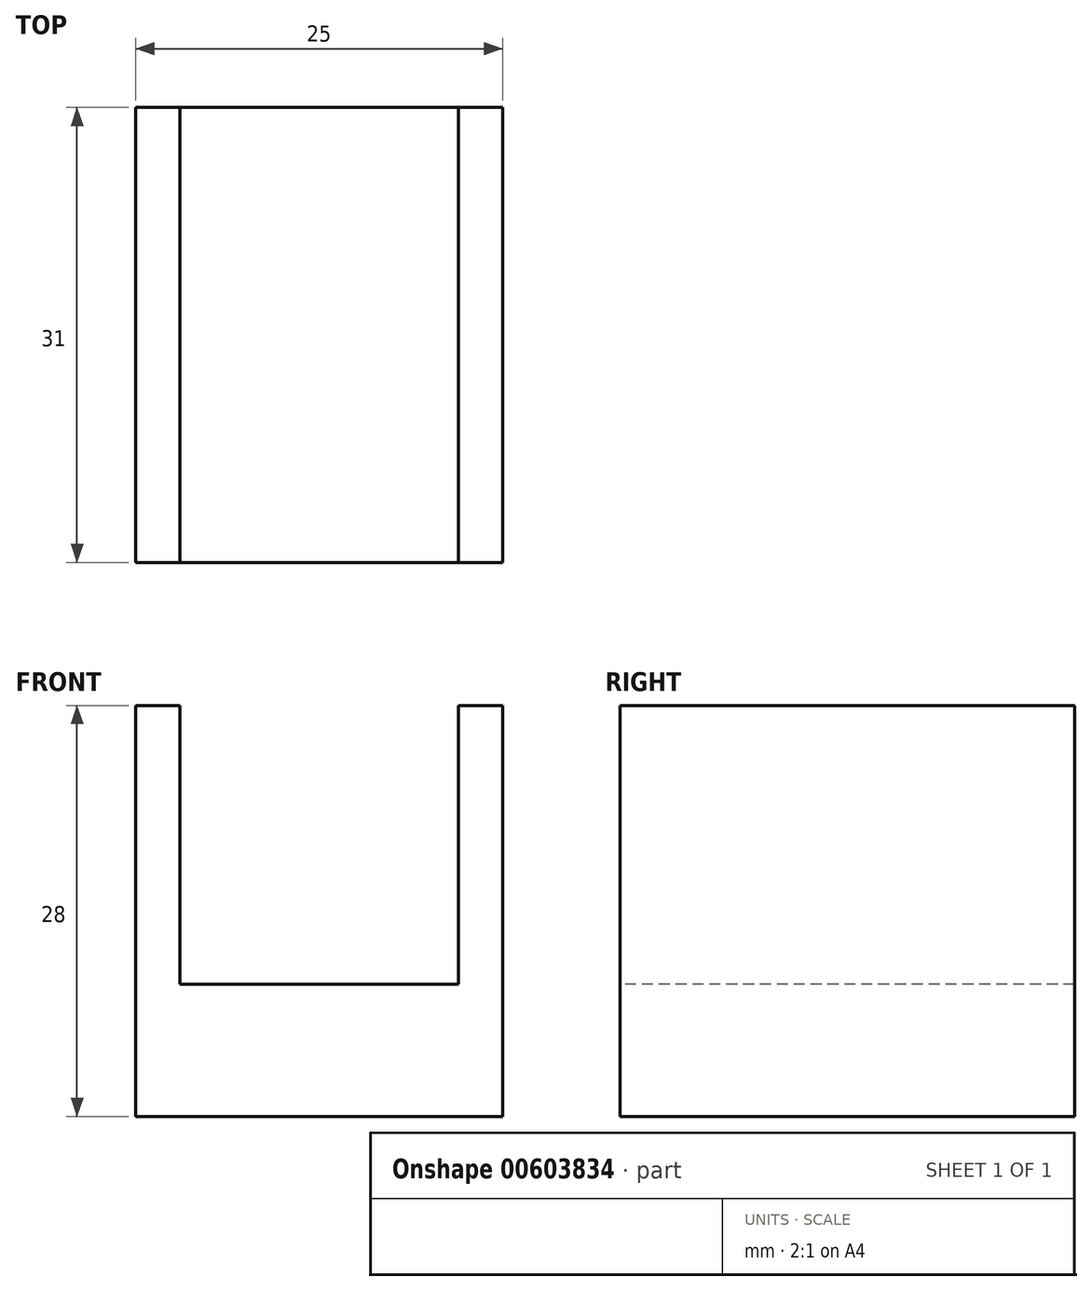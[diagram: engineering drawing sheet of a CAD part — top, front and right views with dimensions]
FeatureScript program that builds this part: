
annotation { "Feature Type Name" : "Feature", "Feature Type Description" : "" }
export const myFeature = defineFeature(function(context is Context, id is Id, definition is map)
    precondition{}
    {
        {
            var Q0;
            Q0=qCreatedBy(makeId("Top.planeOp"),FACE);
            var sketch = newSketch(context, id + "F0", { "sketchPlane" : qUnion([Q0])});
            skLineSegment(sketch, "E0.bottom", {"start": v(0, 0) * mm, "end": v(25, 0) * mm});
            skLineSegment(sketch, "E0.top", {"start": v(0, 31) * mm, "end": v(25, 31) * mm});
            skLineSegment(sketch, "E0.left", {"start": v(0, 0) * mm, "end": v(0, 31) * mm});
            skLineSegment(sketch, "E0.right", {"start": v(25, 0) * mm, "end": v(25, 31) * mm});
            skSolve(sketch);
        }
        {
            var Q0;
            Q0=makeQuery(id+"F0.imprint","IMPRINT",FACE,{"disambiguationData":[TD([[makeQuery(id+"F0.imprint","IMPRINT",EDGE,{"derivedFrom":sQuery(id+"F0.wireOp",EDGE,"E0.bottom")}),1.0]])]});
            extrude(context, id + "F1", {"entities" : qUnion([Q0]), "depth" : 28 * mm, "offsetDistance" : 25 * mm});
        }
        {
            var Q0;
            Q0=makeQuery(id+"F1.opExtrude","SWEPT_FACE",FACE,{"disambiguationData":[OSD([sQuery(id+"F0.wireOp",EDGE,"E0.bottom")])]});
            var sketch = newSketch(context, id + "F2", { "sketchPlane" : qUnion([Q0])});
            skSolve(sketch);
        }
        {
            var Q0;
            {var subQ0=sQuery(id+"F0.wireOp",EDGE,"E0.bottom");var subQ1=makeQuery(id+"F1.opExtrude","CAP_EDGE",EDGE,{"disambiguationData":[OSD([subQ0])],"isStart":true});Q0=makeQuery(id+"F2.imprint","IMPRINT",FACE,{"disambiguationData":[TD([[makeQuery(id+"F2.imprint","IMPRINT",EDGE,{"derivedFrom":subQ1}),1.0]])]});}
            var sketch = newSketch(context, id + "F3", { "sketchPlane" : qUnion([Q0])});
            skLineSegment(sketch, "E1.bottom", {"start": v(3, 28) * mm, "end": v(22, 28) * mm});
            skLineSegment(sketch, "E1.top", {"start": v(3, 9) * mm, "end": v(22, 9) * mm});
            skLineSegment(sketch, "E1.left", {"start": v(3, 28) * mm, "end": v(3, 9) * mm});
            skLineSegment(sketch, "E1.right", {"start": v(22, 28) * mm, "end": v(22, 9) * mm});
            skSolve(sketch);
        }
        {
            var Q0;
            Q0 = qSketchRegion(id + "F3", true);
            extrude(context, id + "F4", {"entities" : qUnion([Q0]), "operationType" : NewBodyOperationType.REMOVE, "endBound" : BoundingType.THROUGH_ALL, "oppositeDirection" : true, "depth" : 25 * mm, "offsetDistance" : 25 * mm});
        }
    });
